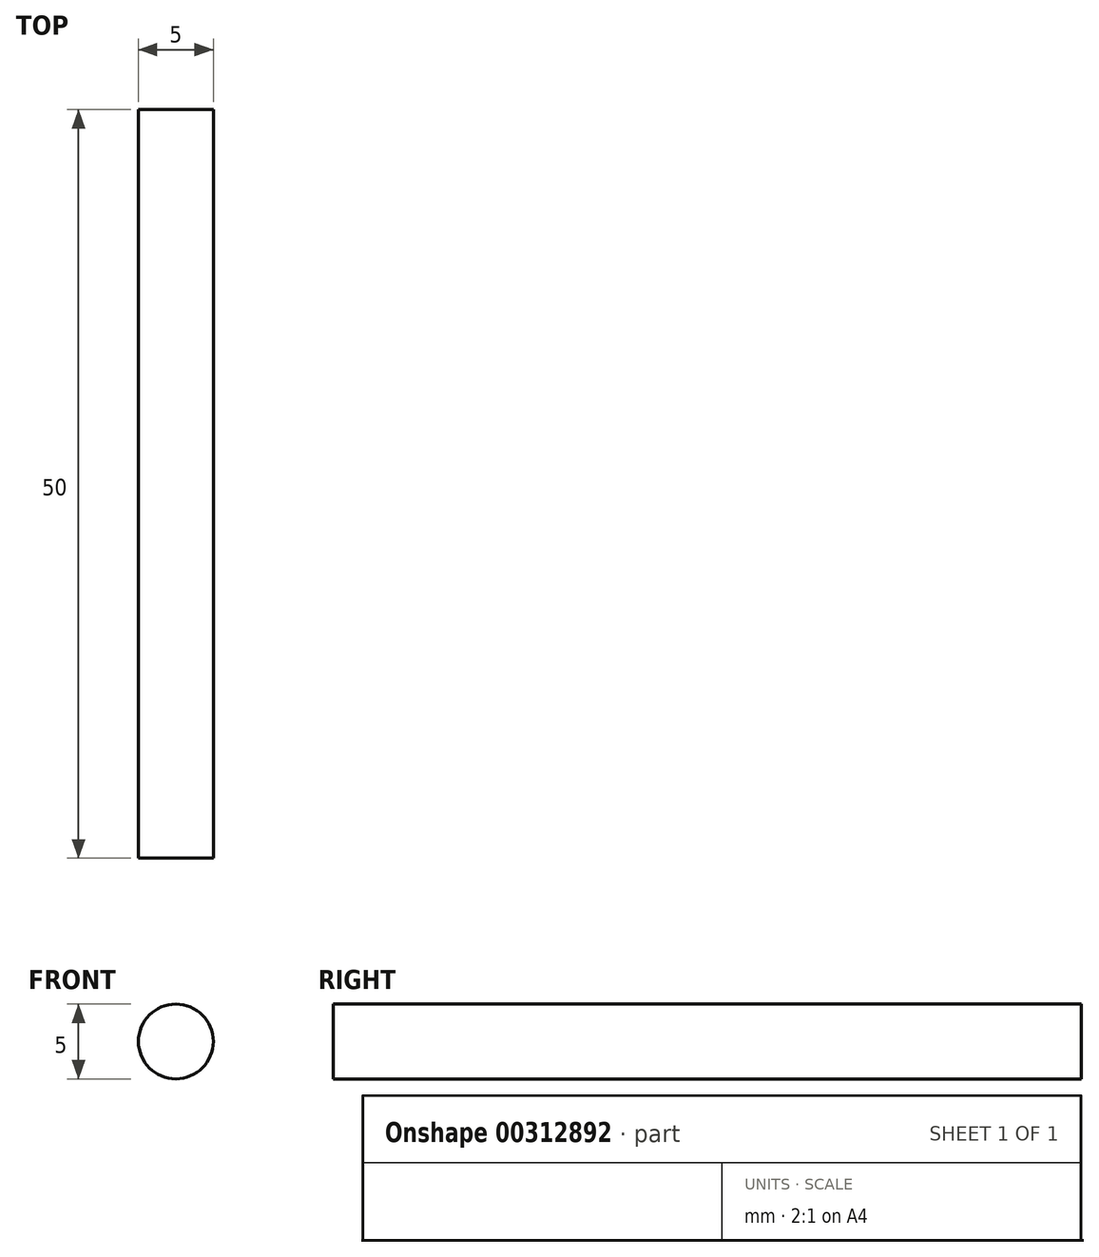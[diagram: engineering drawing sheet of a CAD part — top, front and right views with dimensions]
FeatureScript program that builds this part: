
annotation { "Feature Type Name" : "Feature", "Feature Type Description" : "" }
export const myFeature = defineFeature(function(context is Context, id is Id, definition is map)
    precondition{}
    {
        {
            var Q0;
            Q0=qCreatedBy(makeId("Front.planeOp"),FACE);
            var sketch = newSketch(context, id + "F0", { "sketchPlane" : qUnion([Q0])});
            skCircle(sketch, "E0", {"center": v(0, 0) * mm, "radius": 2.5 * mm});
            skSolve(sketch);
        }
        {
            var Q0;
            Q0 = qSketchRegion(id + "F0", true);
            extrude(context, id + "F1", {"entities" : qUnion([Q0]), "depth" : 50 * mm, "offsetDistance" : 25 * mm});
        }
    });
